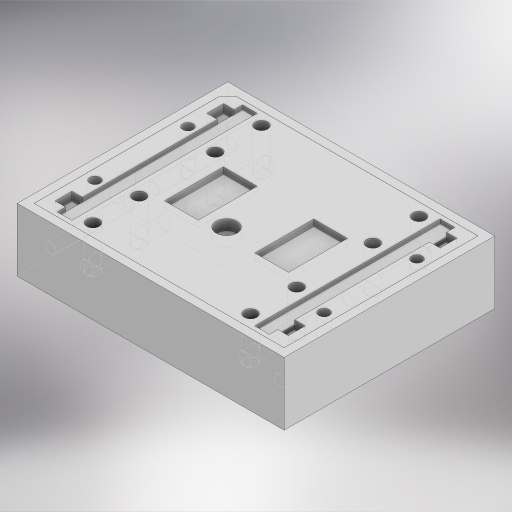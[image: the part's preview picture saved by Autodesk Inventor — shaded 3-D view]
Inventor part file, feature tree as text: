
AUTODESK INVENTOR PART (.ipt)
format: ipt  version: 2024 (Build 280153000, 153)  size: 534,528 bytes
history: native  units: in
note: dims shown in document units (in); Inventor stores cm internally (conversion verified against a paired STEP export)
features: sketch x11, extrude x10, hole x1
ambient origin geometry x8: Origin, YZ Plane, XZ Plane, XY Plane, X Axis, Y Axis, Z Axis, Center Point
bodies: Solid1 (feature_tree)
feature tree (22):
  extrude  "Extrusion1"  Depth=2.5in
  extrude  "Extrusion2"  Depth=1.815in
  extrude  "Extrusion3"  TaperAngle=45.0deg  [1 undecoded]
  extrude  "Extrusion4"  Depth=0.0004in TaperAngle=0.0deg
  extrude  "Extrusion5"  Depth=0.2756in
  extrude  "Extrusion6"  Depth=0.1772in
  extrude  "Extrusion7"  Depth=0.1181in
  hole  "Hole1"  [1 undecoded]
  extrude  "Extrusion8"  Depth=0.0787in
  extrude  "Extrusion9"  Depth=0.1772in
  extrude  "Extrusion10"  Depth=0.3937in
  sketch  "Sketch1"  dims[d0=1.9724in d1=2.5in]
  sketch  "Sketch2"  dims[d2=0.5906in d3=0.0in d4=1.815in]
  sketch  "Sketch3"  dims[d5=2.3425in d6=45.0deg]
  sketch  "Sketch4"  dims[d7=0.0787in d8=0.0004in d9=0.0in]
  sketch  "Sketch5"  dims[d10=0.1181in d11=0.2756in]
  sketch  "Sketch6"  dims[d12=0.0787in d13=0.1772in]
  sketch  "Sketch7"  dims[d14=0.0787in d15=0.1181in]
  sketch  "Sketch8"  dims[d16=0.2756in d17=0.1772in]
  sketch  "Sketch10"  dims[d18=0.1181in d19=0.0787in]
  sketch  "Sketch11"  dims[d20=0.2756in d21=0.1772in]
  sketch  "Sketch12"  dims[d22=0.1181in d23=0.2756in d24=0.0787in d25=0.1772in d26=0.0787in d27=0.0in d28=0.1772in d29=0.315in d30=0.0394in d31=0.0394in d32=0.0394in d33=0.0in d34=0.0394in d35=0.0394in d36=0.1772in d37=0.315in d38=0.5906in d39=0.9055in d40=0.5512in d41=0.5512in d43=0.9055in d44=0.5906in d45=0.0591in d46=0.0in d47=0.1969in d48=0.7087in d49=1.248in d50=0.0984in d51=0.0in d52=0.0984in d53=0.0984in d54=0.0984in d55=0.4724in d56=0.0984in d57=0.4724in d58=0.1181in d59=0.1181in d60=0.1181in d61=0.1181in d63=0.1181in d64=0.1181in d65=0.4331in d66=0.4331in d67=0.4331in d68=0.3937in d69=0.0in d70=0.2362in d71=0.25in d72=0.2362in d73=0.1575in d74=0.0787in d75=90.0deg d76=2.3622in d77=0.0in d78=0.0984in d79=1.4705in d80=0.0in d81=0.1181in d82=0.1181in d83=0.0984in d84=0.1378in d85=0.0in d86=0.1378in d87=0.0in]
note: 2 required parameter values undecoded (feature->parameter linkage not recoverable at this tier; creation-order binding heuristic only, values carry confidence <= 0.55)
